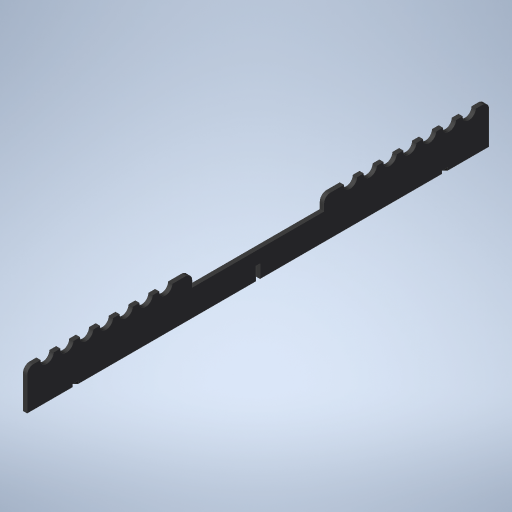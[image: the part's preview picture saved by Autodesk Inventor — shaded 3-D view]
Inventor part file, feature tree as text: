
AUTODESK INVENTOR PART (.ipt)
format: ipt  version: 2024.3 (Build 283343000, 343)  size: 361,984 bytes
history: native  units: mm
features: extrude x4, sketch x4, projected_geometry x3, fillet x2, mirror x1
ambient origin geometry x8: Origin, YZ Plane, XZ Plane, XY Plane, X Axis, Y Axis, Z Axis, Center Point
bodies: Solid1 (feature_tree)
feature tree (14):
  extrude  "Extrusion1"  Depth=350.0mm
  extrude  "Extrusion2"  Depth=100.0mm
  extrude  "Extrusion3"  Depth=10.0mm
  fillet  "Fillet1"  Radius=3.0mm
  fillet  "Fillet2"  Radius=3.1mm
  mirror  "Mirror1"
  extrude  "Extrusion5"  Depth=3.0mm TaperAngle=0.0deg
  sketch  "Sketch1"  dims[d0=30.0mm d1=350.0mm]
  sketch  "Sketch2"  dims[d2=0.0mm d3=100.0mm]
  projected_geometry  "Projected Loop1"
  sketch  "Sketch3"  dims[d4=0.0mm d5=10.0mm d6=3.0mm d7=0.0mm d8=3.1mm]
  sketch  "Sketch6"  dims[d9=20.0mm d10=3.0mm d11=0.0mm d12=10.0mm d13=10.0mm d14=10.0mm d16=10.0mm d17=10.0mm d18=10.0mm d19=15.0mm d20=15.0mm d21=15.0mm d22=15.0mm d23=15.0mm d24=15.0mm d25=10.0mm d26=15.0mm d27=3.0mm d28=0.0mm d29=5.0mm d30=5.0mm d42=45.0deg d43=3.0mm d44=3.0mm d45=195.0mm d47=2.0mm d48=0.0mm d50=97.5mm]
  projected_geometry  "Projected Loop7"
  projected_geometry  "Projected Loop8"
